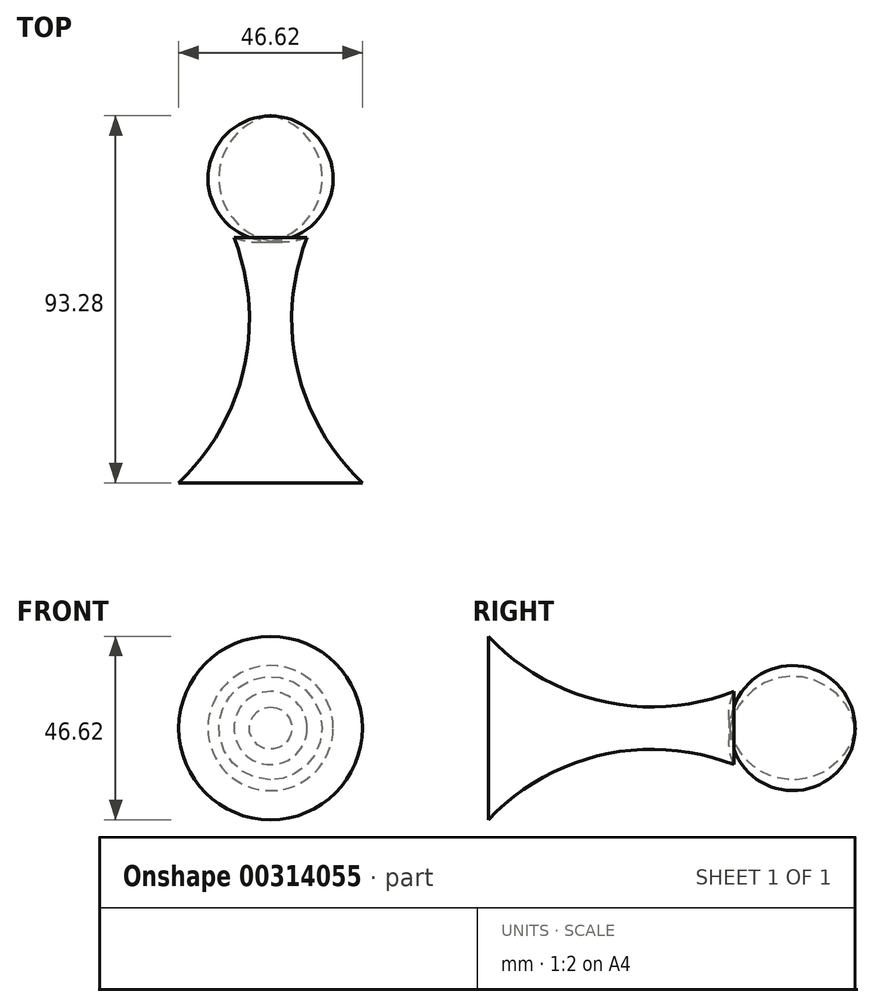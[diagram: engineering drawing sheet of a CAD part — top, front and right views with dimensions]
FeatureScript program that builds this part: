
annotation { "Feature Type Name" : "Feature", "Feature Type Description" : "" }
export const myFeature = defineFeature(function(context is Context, id is Id, definition is map)
    precondition{}
    {
        {
            var Q0;
            Q0=qCreatedBy(makeId("Top.planeOp"),FACE);
            var sketch = newSketch(context, id + "F0", { "sketchPlane" : qUnion([Q0])});
            skLineSegment(sketch, "E0", {"start": v(0, 54.98) * mm, "end": v(0, -38.23) * mm});
            skArc(sketch, "E1", {"start": v(0, 23.2) * mm, "mid": v(15.9, 39.09) * mm, "end": v(0, 54.98) * mm});
            skArc(sketch, "E2", {"start": v(0, 23.2) * mm, "mid": v(4.71, 22.98) * mm, "end": v(9.29, 24.13) * mm});
            skArc(sketch, "E3", {"start": v(9.29, 24.13) * mm, "mid": v(6.78, -9.19) * mm, "end": v(23.3, -38.23) * mm});
            skLineSegment(sketch, "E4", {"start": v(23.3, -38.23) * mm, "end": v(0, -38.23) * mm});
            skSolve(sketch);
        }
        {
            var Q0;
            Q0 = qSketchRegion(id + "F0", true);
            var Q1;
            Q1=sQuery(id+"F0.wireOp",EDGE,"E0");
            revolve(context, id + "F1", {"entities" : qUnion([Q0]), "axis" : qUnion([Q1]), "revolveType" : RevolveType.FULL});
        }
    });
